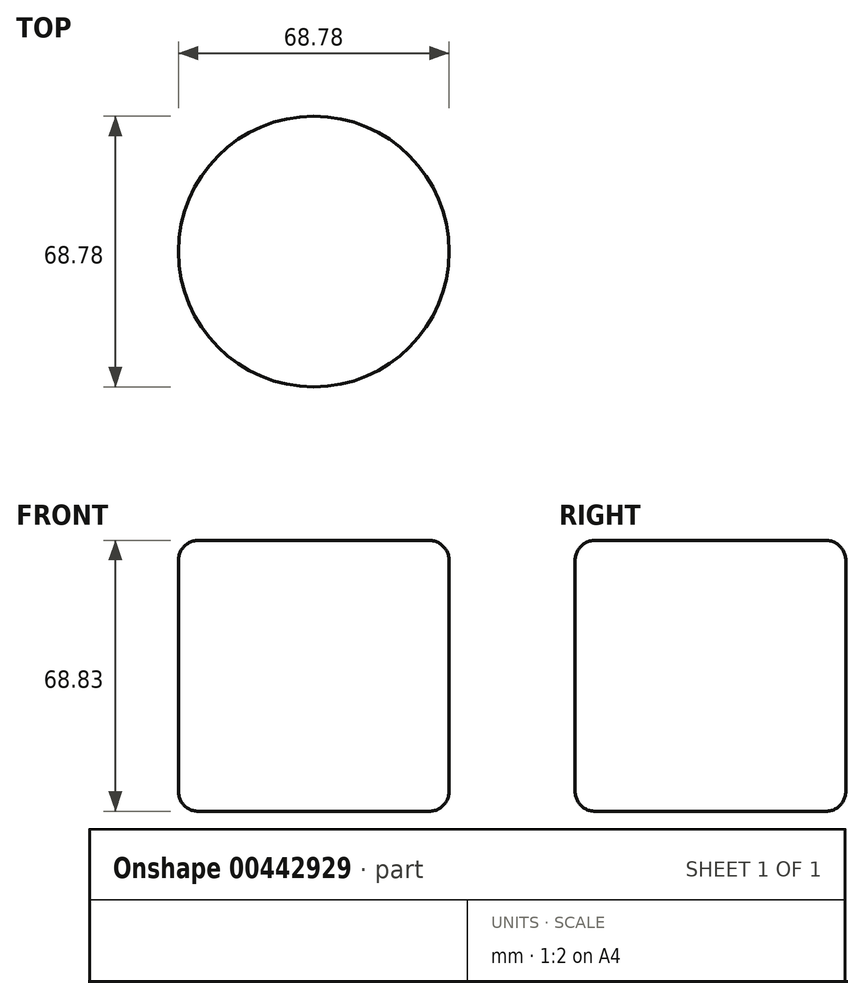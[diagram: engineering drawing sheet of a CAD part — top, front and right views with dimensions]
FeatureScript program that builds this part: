
annotation { "Feature Type Name" : "Feature", "Feature Type Description" : "" }
export const myFeature = defineFeature(function(context is Context, id is Id, definition is map)
    precondition{}
    {
        {
            var Q0;
            Q0=qCreatedBy(makeId("Top.planeOp"),FACE);
            var sketch = newSketch(context, id + "F0", { "sketchPlane" : qUnion([Q0])});
            skCircle(sketch, "E0", {"center": v(0, 0) * mm, "radius": 34.39 * mm});
            skSolve(sketch);
        }
        {
            var Q0;
            Q0=makeQuery(id+"F0.imprint","IMPRINT",FACE,{"disambiguationData":[TD([[makeQuery(id+"F0.imprint","IMPRINT",EDGE,{"derivedFrom":sQuery(id+"F0.wireOp",EDGE,"E0")}),1.0]])]});
            extrude(context, id + "F1", {"entities" : qUnion([Q0]), "depth" : 68.83 * mm});
        }
        {
            var Q0;
            Q0=makeQuery(id+"F1.opExtrude","CAP_FACE",FACE,{"disambiguationData":[OSD([sQuery(id+"F0.wireOp",EDGE,"E0")])],"isStart":false});
            fillet(context, id + "F2", {"entities" : qUnion([Q0]), "radius" : 5.08 * mm, "tangentPropagation" : true, "allowEdgeOverflow" : false});
        }
        {
            var Q0;
            Q0=makeQuery(id+"F1.opExtrude","SWEPT_FACE",FACE,{"disambiguationData":[OSD([sQuery(id+"F0.wireOp",EDGE,"E0")])]});
            fillet(context, id + "F3", {"entities" : qUnion([Q0]), "radius" : 5.08 * mm, "tangentPropagation" : true, "allowEdgeOverflow" : false});
        }
    });
